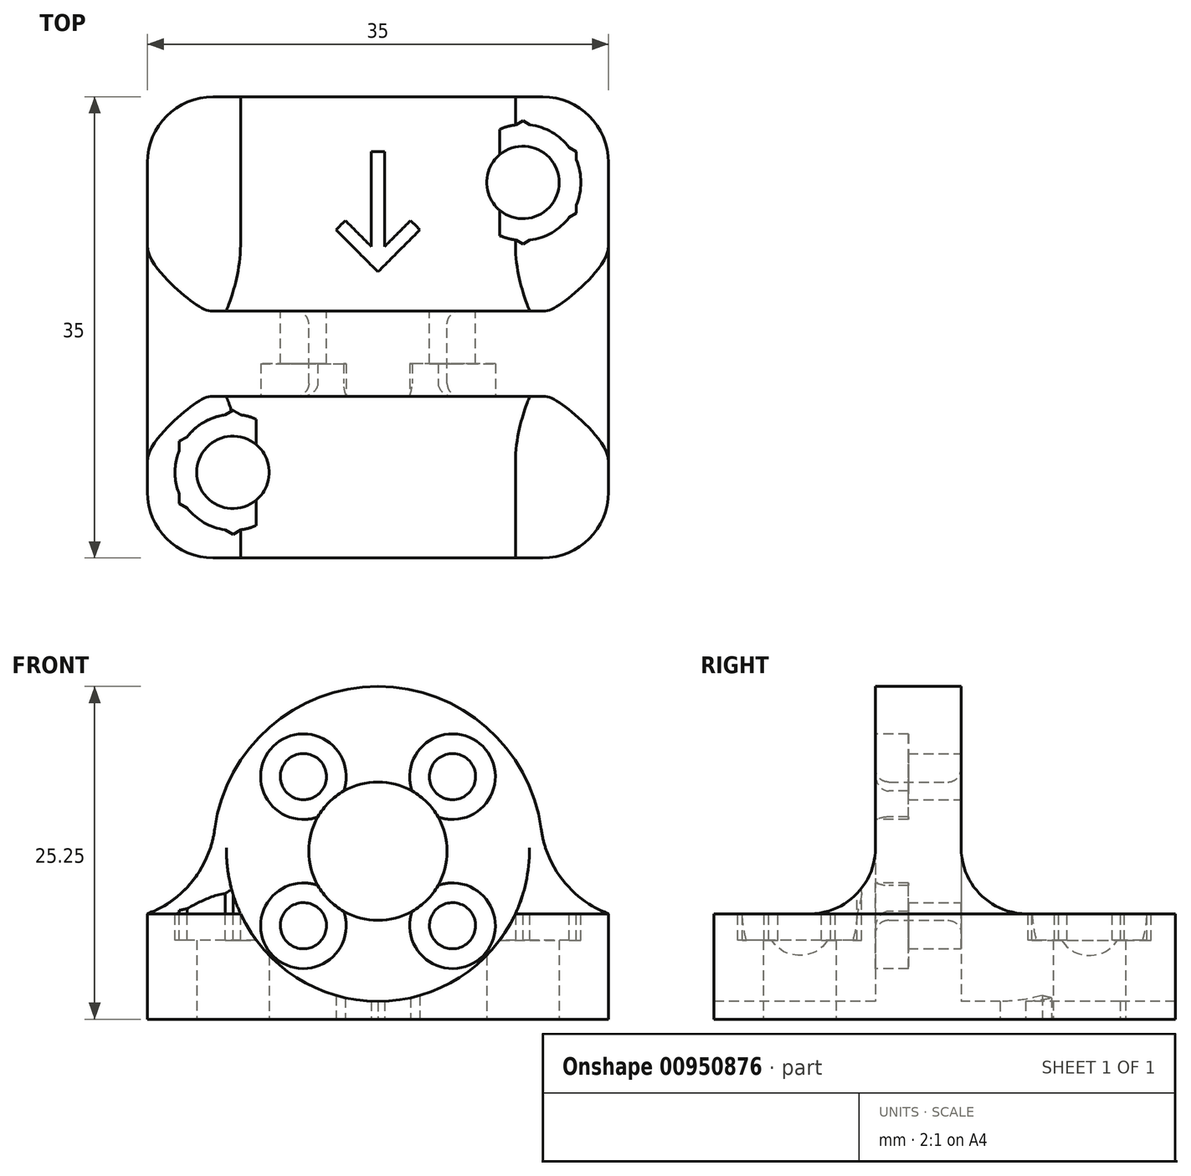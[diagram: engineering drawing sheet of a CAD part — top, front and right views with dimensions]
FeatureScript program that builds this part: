
annotation { "Feature Type Name" : "Feature", "Feature Type Description" : "" }
export const myFeature = defineFeature(function(context is Context, id is Id, definition is map)
    precondition{}
    {
        {
            var Q0;
            Q0=qCreatedBy(makeId("Front.planeOp"),FACE);
            cPlane(context, id + "F0", {"entities" : qUnion([Q0]), "cplaneType" : CPlaneType.OFFSET, "offset" : 2 * mm, "width" : 150 * mm, "height" : 150 * mm});
        }
        {
            var Q0;
            Q0=qCreatedBy(makeId("Top.planeOp"),FACE);
            var sketch = newSketch(context, id + "F1", { "sketchPlane" : qUnion([Q0])});
            skLineSegment(sketch, "E0.bottom", {"start": v(-17.5, 17.5) * mm, "end": v(17.5, 17.5) * mm});
            skLineSegment(sketch, "E0.top", {"start": v(-17.5, -17.5) * mm, "end": v(17.5, -17.5) * mm});
            skLineSegment(sketch, "E0.left", {"start": v(-17.5, 17.5) * mm, "end": v(-17.5, -17.5) * mm});
            skLineSegment(sketch, "E0.right", {"start": v(17.5, 17.5) * mm, "end": v(17.5, -17.5) * mm});
            skPoint(sketch, "E0.middle", {"position": v(0, 0) * mm});
            skLineSegment(sketch, "E1.bottom", {"start": v(-11, 11) * mm, "end": v(11, 11) * mm, "construction": true});
            skLineSegment(sketch, "E1.top", {"start": v(-11, -11) * mm, "end": v(11, -11) * mm, "construction": true});
            skLineSegment(sketch, "E1.left", {"start": v(-11, 11) * mm, "end": v(-11, -11) * mm, "construction": true});
            skLineSegment(sketch, "E1.right", {"start": v(11, 11) * mm, "end": v(11, -11) * mm, "construction": true});
            skCircle(sketch, "E2", {"center": v(-11, 11) * mm, "radius": 2.75 * mm, "construction": true});
            skCircle(sketch, "E3", {"center": v(11, 11) * mm, "radius": 2.75 * mm});
            skCircle(sketch, "E4", {"center": v(11, -11) * mm, "radius": 2.75 * mm, "construction": true});
            skCircle(sketch, "E5", {"center": v(-11, -11) * mm, "radius": 2.75 * mm});
            skSolve(sketch);
        }
        {
            var Q0;
            Q0=qSketchRegion(id+"F1",true);
            extrude(context, id + "F2", {"entities" : qUnion([Q0]), "depth" : 8 * mm, "offsetDistance" : 25 * mm});
        }
        {
            var Q0;
            Q0=qCreatedBy(id+"F0.planeOp",FACE);
            var sketch = newSketch(context, id + "F3", { "sketchPlane" : qUnion([Q0])});
            skLineSegment(sketch, "E6", {"start": v(0, 0) * mm, "end": v(0, 12.75) * mm, "construction": true});
            skArc(sketch, "E7", {"start": v(12.5, 12.75) * mm, "mid": v(0, 25.25) * mm, "end": v(-12.5, 12.75) * mm});
            skLineSegment(sketch, "E8", {"start": v(-12.5, 12.75) * mm, "end": v(-12.5, 0) * mm});
            skLineSegment(sketch, "E9.MirrorCS", {"start": v(12.5, 12.75) * mm, "end": v(12.5, 0) * mm});
            skCircle(sketch, "E10", {"center": v(0, 12.75) * mm, "radius": 5.25 * mm});
            skCircle(sketch, "E11", {"center": v(0, 12.75) * mm, "radius": 8 * mm, "construction": true});
            skLineSegment(sketch, "E12", {"start": v(0, 20.75) * mm, "end": v(0, 4.75) * mm, "construction": true});
            skPoint(sketch, "E12.startSnap0", {"position": v(0, 25.25) * mm});
            skLineSegment(sketch, "E13", {"start": v(-8, 12.75) * mm, "end": v(8, 12.75) * mm, "construction": true});
            skLineSegment(sketch, "E14", {"start": v(0, 12.75) * mm, "end": v(-5.66, 18.4) * mm, "construction": true});
            skLineSegment(sketch, "E15", {"start": v(0, 12.75) * mm, "end": v(-5.66, 7.1) * mm, "construction": true});
            skLineSegment(sketch, "E16.MirrorCS", {"start": v(0, 12.75) * mm, "end": v(5.66, 18.4) * mm, "construction": true});
            skLineSegment(sketch, "E17.MirrorCS", {"start": v(0, 12.75) * mm, "end": v(5.66, 7.1) * mm, "construction": true});
            skCircle(sketch, "E18", {"center": v(-5.66, 18.4) * mm, "radius": 1.75 * mm});
            skCircle(sketch, "E19", {"center": v(-5.66, 7.1) * mm, "radius": 1.75 * mm});
            skCircle(sketch, "E20", {"center": v(5.66, 7.1) * mm, "radius": 1.75 * mm});
            skCircle(sketch, "E21", {"center": v(5.66, 18.4) * mm, "radius": 1.75 * mm});
            skLineSegment(sketch, "E22", {"start": v(-12.5, 0) * mm, "end": v(12.5, 0) * mm});
            skSolve(sketch);
        }
        {
            var Q0;
            Q0=qCreatedBy(makeId("Front.planeOp"),FACE);
            var sketch = newSketch(context, id + "F4", { "sketchPlane" : qUnion([Q0])});
            skLineSegment(sketch, "E23", {"start": v(0, 0) * mm, "end": v(0, 12.85) * mm, "construction": true});
            skCircle(sketch, "E24", {"center": v(0, 12.85) * mm, "radius": 11.5 * mm});
            skSolve(sketch);
        }
        {
            var Q0;
            Q0=qSketchRegion(id+"F4",true);
            extrude(context, id + "F5", {"entities" : qUnion([Q0]), "operationType" : NewBodyOperationType.REMOVE, "endBound" : BoundingType.SYMMETRIC, "oppositeDirection" : true, "depth" : 36 * mm, "offsetDistance" : 25 * mm});
        }
        {
            var Q0;
            Q0 = qSketchRegion(id + "F3", true);
            extrude(context, id + "F6", {"entities" : qUnion([Q0]), "operationType" : NewBodyOperationType.ADD, "endBound" : BoundingType.SYMMETRIC, "depth" : 6.5 * mm, "offsetDistance" : 25 * mm});
        }
        {
            var Q0;
            {var subQ0=sQuery(id+"F1.wireOp",EDGE,"E4");var subQ1=sQuery(id+"F1.wireOp",EDGE,"E0.top");var subQ2=sQuery(id+"F1.wireOp",EDGE,"E0.right");var subQ3=sQuery(id+"F1.wireOp",EDGE,"E0.bottom");Q0=makeQuery(id+"F6.boolean.opBoolean","INTERSECT",EDGE,{"derivedFrom":[makeQuery(id+"F5.boolean.opBoolean","SPLIT",FACE,{"disambiguationData":[TD([makeQuery(id+"F2.opExtrude","SWEPT_FACE",FACE,{"disambiguationData":[OSD([subQ2])]})])],"derivedFrom":makeQuery(id+"F2.opExtrude","CAP_FACE",FACE,{"disambiguationData":[OSD([subQ3,subQ1,sQuery(id+"F1.wireOp",EDGE,"E0.left"),subQ2,sQuery(id+"F1.wireOp",EDGE,"E2"),subQ0])],"isStart":false})}),makeQuery(id+"F6.opExtrude","SWEPT_FACE",FACE,{"disambiguationData":[OSD([sQuery(id+"F3.wireOp",EDGE,"E9.MirrorCS")])]})]});}
            var Q1;
            {var subQ0=sQuery(id+"F1.wireOp",EDGE,"E2");var subQ1=sQuery(id+"F1.wireOp",EDGE,"E0.left");var subQ2=sQuery(id+"F1.wireOp",EDGE,"E0.top");var subQ3=sQuery(id+"F1.wireOp",EDGE,"E0.bottom");Q1=makeQuery(id+"F6.boolean.opBoolean","INTERSECT",EDGE,{"derivedFrom":[makeQuery(id+"F5.boolean.opBoolean","SPLIT",FACE,{"disambiguationData":[TD([makeQuery(id+"F2.opExtrude","SWEPT_FACE",FACE,{"disambiguationData":[OSD([subQ1])]})])],"derivedFrom":makeQuery(id+"F2.opExtrude","CAP_FACE",FACE,{"disambiguationData":[OSD([subQ3,subQ2,subQ1,sQuery(id+"F1.wireOp",EDGE,"E0.right"),subQ0,sQuery(id+"F1.wireOp",EDGE,"E4")])],"isStart":false})}),makeQuery(id+"F6.opExtrude","SWEPT_FACE",FACE,{"disambiguationData":[OSD([sQuery(id+"F3.wireOp",EDGE,"E8")])]})]});}
            fillet(context, id + "F7", {"entities" : qUnion([Q0, Q1]), "radius" : 8 * mm, "tangentPropagation" : true, "allowEdgeOverflow" : false});
        }
        {
            var Q0;
            {var subQ0=sQuery(id+"F1.wireOp",EDGE,"E2");var subQ1=sQuery(id+"F1.wireOp",EDGE,"E0.left");var subQ2=sQuery(id+"F1.wireOp",EDGE,"E0.top");var subQ3=sQuery(id+"F1.wireOp",EDGE,"E0.bottom");Q0=makeQuery(id+"F7.opFillet","SPLIT",FACE,{"disambiguationData":[OD(0.0)],"derivedFrom":makeQuery(id+"F5.boolean.opBoolean","SPLIT",FACE,{"disambiguationData":[TD([makeQuery(id+"F2.opExtrude","SWEPT_FACE",FACE,{"disambiguationData":[OSD([subQ1])]})])],"derivedFrom":makeQuery(id+"F2.opExtrude","CAP_FACE",FACE,{"disambiguationData":[OSD([subQ3,subQ2,subQ1,sQuery(id+"F1.wireOp",EDGE,"E0.right"),subQ0,sQuery(id+"F1.wireOp",EDGE,"E4")])],"isStart":false})})});}
            var sketch = newSketch(context, id + "F8", { "sketchPlane" : qUnion([Q0])});
            skPoint(sketch, "E25.0.midPoint.positionSnap0", {"position": v(5.2, -11) * mm});
            skLineSegment(sketch, "E26", {"start": v(17.5, 17.5) * mm, "end": v(-17.5, -17.5) * mm, "construction": true});
            skCircle(sketch, "E27.cCircle", {"center": v(11, 11) * mm, "radius": 4.05 * mm, "construction": true});
            skLineSegment(sketch, "E27.0", {"start": v(15.05, 13.34) * mm, "end": v(15.05, 8.66) * mm});
            skLineSegment(sketch, "E27.1", {"start": v(15.05, 8.66) * mm, "end": v(11, 6.32) * mm});
            skLineSegment(sketch, "E27.2", {"start": v(11, 6.32) * mm, "end": v(6.95, 8.66) * mm});
            skLineSegment(sketch, "E27.3", {"start": v(6.95, 8.66) * mm, "end": v(6.95, 13.34) * mm});
            skLineSegment(sketch, "E27.4", {"start": v(6.95, 13.34) * mm, "end": v(11, 15.68) * mm});
            skLineSegment(sketch, "E27.5", {"start": v(11, 15.68) * mm, "end": v(15.05, 13.34) * mm});
            skPoint(sketch, "E27.0.midPoint", {"position": v(15.05, 11) * mm});
            skCircle(sketch, "E28.cCircle", {"center": v(-11, -11) * mm, "radius": 4.08 * mm, "construction": true});
            skLineSegment(sketch, "E28.0", {"start": v(-11, -6.3) * mm, "end": v(-6.93, -8.65) * mm});
            skLineSegment(sketch, "E28.1", {"start": v(-6.93, -8.65) * mm, "end": v(-6.93, -13.35) * mm});
            skLineSegment(sketch, "E28.2", {"start": v(-6.93, -13.35) * mm, "end": v(-11, -15.7) * mm});
            skLineSegment(sketch, "E28.3", {"start": v(-11, -15.7) * mm, "end": v(-15.08, -13.35) * mm});
            skLineSegment(sketch, "E28.4", {"start": v(-15.07, -13.35) * mm, "end": v(-15.07, -8.65) * mm});
            skLineSegment(sketch, "E28.5", {"start": v(-15.07, -8.65) * mm, "end": v(-11, -6.3) * mm});
            skPoint(sketch, "E28.0.midPoint", {"position": v(-8.96, -7.47) * mm});
            skSolve(sketch);
        }
        {
            var Q0;
            Q0=qSketchRegion(id+"F8",true);
            extrude(context, id + "F9", {"entities" : qUnion([Q0]), "operationType" : NewBodyOperationType.REMOVE, "oppositeDirection" : true, "depth" : 2 * mm, "offsetDistance" : 25 * mm});
        }
        {
            var Q0;
            {var subQ0=sQuery(id+"F1.wireOp",EDGE,"E2");var subQ1=sQuery(id+"F1.wireOp",EDGE,"E0.left");var subQ2=sQuery(id+"F1.wireOp",EDGE,"E0.top");var subQ3=sQuery(id+"F1.wireOp",EDGE,"E0.bottom");Q0=makeQuery(id+"F7.opFillet","SPLIT",FACE,{"disambiguationData":[OD(0.0)],"derivedFrom":makeQuery(id+"F5.boolean.opBoolean","SPLIT",FACE,{"disambiguationData":[TD([makeQuery(id+"F2.opExtrude","SWEPT_FACE",FACE,{"disambiguationData":[OSD([subQ1])]})])],"derivedFrom":makeQuery(id+"F2.opExtrude","CAP_FACE",FACE,{"disambiguationData":[OSD([subQ3,subQ2,subQ1,sQuery(id+"F1.wireOp",EDGE,"E0.right"),subQ0,sQuery(id+"F1.wireOp",EDGE,"E4")])],"isStart":false})})});}
            var sketch = newSketch(context, id + "F10", { "sketchPlane" : qUnion([Q0])});
            skCircle(sketch, "E29", {"center": v(11, 11) * mm, "radius": 4.4 * mm});
            skCircle(sketch, "E30", {"center": v(-11, -11) * mm, "radius": 4.4 * mm});
            skSolve(sketch);
        }
        {
            var Q0;
            Q0=qSketchRegion(id+"F10",true);
            extrude(context, id + "F11", {"entities" : qUnion([Q0]), "operationType" : NewBodyOperationType.REMOVE, "oppositeDirection" : true, "depth" : 2 * mm, "offsetDistance" : 25 * mm});
        }
        {
            var Q0;
            {var subQ0=sQuery(id+"F1.wireOp",EDGE,"E4");var subQ1=sQuery(id+"F1.wireOp",EDGE,"E0.top");var subQ2=sQuery(id+"F1.wireOp",EDGE,"E0.right");var subQ3=sQuery(id+"F1.wireOp",EDGE,"E0.bottom");Q0=makeQuery(id+"F6.boolean.opBoolean","INTERSECT",EDGE,{"derivedFrom":[makeQuery(id+"F5.boolean.opBoolean","SPLIT",FACE,{"disambiguationData":[TD([makeQuery(id+"F2.opExtrude","SWEPT_FACE",FACE,{"disambiguationData":[OSD([subQ2])]})])],"derivedFrom":makeQuery(id+"F2.opExtrude","CAP_FACE",FACE,{"disambiguationData":[OSD([subQ3,subQ1,sQuery(id+"F1.wireOp",EDGE,"E0.left"),subQ2,sQuery(id+"F1.wireOp",EDGE,"E2"),subQ0])],"isStart":false})}),makeQuery(id+"F6.opExtrude","CAP_FACE",FACE,{"disambiguationData":[OSD([sQuery(id+"F3.wireOp",EDGE,"E7"),sQuery(id+"F3.wireOp",EDGE,"E8"),sQuery(id+"F3.wireOp",EDGE,"E9.MirrorCS"),sQuery(id+"F3.wireOp",EDGE,"E10"),sQuery(id+"F3.wireOp",EDGE,"E18"),sQuery(id+"F3.wireOp",EDGE,"E19"),sQuery(id+"F3.wireOp",EDGE,"E20"),sQuery(id+"F3.wireOp",EDGE,"E21"),sQuery(id+"F3.wireOp",EDGE,"E22")])],"isStart":true})]});}
            var Q1;
            {var subQ0=sQuery(id+"F1.wireOp",EDGE,"E2");var subQ1=sQuery(id+"F1.wireOp",EDGE,"E0.left");var subQ2=sQuery(id+"F1.wireOp",EDGE,"E0.top");var subQ3=sQuery(id+"F1.wireOp",EDGE,"E0.bottom");Q1=makeQuery(id+"F6.boolean.opBoolean","INTERSECT",EDGE,{"derivedFrom":[makeQuery(id+"F5.boolean.opBoolean","SPLIT",FACE,{"disambiguationData":[TD([makeQuery(id+"F2.opExtrude","SWEPT_FACE",FACE,{"disambiguationData":[OSD([subQ1])]})])],"derivedFrom":makeQuery(id+"F2.opExtrude","CAP_FACE",FACE,{"disambiguationData":[OSD([subQ3,subQ2,subQ1,sQuery(id+"F1.wireOp",EDGE,"E0.right"),subQ0,sQuery(id+"F1.wireOp",EDGE,"E4")])],"isStart":false})}),makeQuery(id+"F6.opExtrude","CAP_FACE",FACE,{"disambiguationData":[OSD([sQuery(id+"F3.wireOp",EDGE,"E7"),sQuery(id+"F3.wireOp",EDGE,"E8"),sQuery(id+"F3.wireOp",EDGE,"E9.MirrorCS"),sQuery(id+"F3.wireOp",EDGE,"E10"),sQuery(id+"F3.wireOp",EDGE,"E18"),sQuery(id+"F3.wireOp",EDGE,"E19"),sQuery(id+"F3.wireOp",EDGE,"E20"),sQuery(id+"F3.wireOp",EDGE,"E21"),sQuery(id+"F3.wireOp",EDGE,"E22")])],"isStart":true})]});}
            var Q2;
            {var subQ0=sQuery(id+"F1.wireOp",EDGE,"E2");var subQ1=sQuery(id+"F1.wireOp",EDGE,"E0.left");var subQ2=sQuery(id+"F1.wireOp",EDGE,"E0.top");var subQ3=sQuery(id+"F1.wireOp",EDGE,"E0.bottom");Q2=makeQuery(id+"F6.boolean.opBoolean","INTERSECT",EDGE,{"derivedFrom":[makeQuery(id+"F5.boolean.opBoolean","SPLIT",FACE,{"disambiguationData":[TD([makeQuery(id+"F2.opExtrude","SWEPT_FACE",FACE,{"disambiguationData":[OSD([subQ1])]})])],"derivedFrom":makeQuery(id+"F2.opExtrude","CAP_FACE",FACE,{"disambiguationData":[OSD([subQ3,subQ2,subQ1,sQuery(id+"F1.wireOp",EDGE,"E0.right"),subQ0,sQuery(id+"F1.wireOp",EDGE,"E4")])],"isStart":false})}),makeQuery(id+"F6.opExtrude","CAP_FACE",FACE,{"disambiguationData":[OSD([sQuery(id+"F3.wireOp",EDGE,"E7"),sQuery(id+"F3.wireOp",EDGE,"E8"),sQuery(id+"F3.wireOp",EDGE,"E9.MirrorCS"),sQuery(id+"F3.wireOp",EDGE,"E10"),sQuery(id+"F3.wireOp",EDGE,"E18"),sQuery(id+"F3.wireOp",EDGE,"E19"),sQuery(id+"F3.wireOp",EDGE,"E20"),sQuery(id+"F3.wireOp",EDGE,"E21"),sQuery(id+"F3.wireOp",EDGE,"E22")])],"isStart":false})]});}
            var Q3;
            {var subQ0=sQuery(id+"F1.wireOp",EDGE,"E4");var subQ1=sQuery(id+"F1.wireOp",EDGE,"E0.top");var subQ2=sQuery(id+"F1.wireOp",EDGE,"E0.right");var subQ3=sQuery(id+"F1.wireOp",EDGE,"E0.bottom");Q3=makeQuery(id+"F6.boolean.opBoolean","INTERSECT",EDGE,{"derivedFrom":[makeQuery(id+"F5.boolean.opBoolean","SPLIT",FACE,{"disambiguationData":[TD([makeQuery(id+"F2.opExtrude","SWEPT_FACE",FACE,{"disambiguationData":[OSD([subQ2])]})])],"derivedFrom":makeQuery(id+"F2.opExtrude","CAP_FACE",FACE,{"disambiguationData":[OSD([subQ3,subQ1,sQuery(id+"F1.wireOp",EDGE,"E0.left"),subQ2,sQuery(id+"F1.wireOp",EDGE,"E2"),subQ0])],"isStart":false})}),makeQuery(id+"F6.opExtrude","CAP_FACE",FACE,{"disambiguationData":[OSD([sQuery(id+"F3.wireOp",EDGE,"E7"),sQuery(id+"F3.wireOp",EDGE,"E8"),sQuery(id+"F3.wireOp",EDGE,"E9.MirrorCS"),sQuery(id+"F3.wireOp",EDGE,"E10"),sQuery(id+"F3.wireOp",EDGE,"E18"),sQuery(id+"F3.wireOp",EDGE,"E19"),sQuery(id+"F3.wireOp",EDGE,"E20"),sQuery(id+"F3.wireOp",EDGE,"E21"),sQuery(id+"F3.wireOp",EDGE,"E22")])],"isStart":false})]});}
            var Q4;
            Q4=makeQuery(id+"F2.opExtrude","SWEPT_EDGE",EDGE,{"disambiguationData":[OSD([sQuery(id+"F1.wireOp",EDGE,"E0.top"),sQuery(id+"F1.wireOp",EDGE,"E0.left")])]});
            var Q5;
            Q5=makeQuery(id+"F2.opExtrude","SWEPT_EDGE",EDGE,{"disambiguationData":[OSD([sQuery(id+"F1.wireOp",EDGE,"E0.bottom"),sQuery(id+"F1.wireOp",EDGE,"E0.left")])]});
            var Q6;
            Q6=makeQuery(id+"F2.opExtrude","SWEPT_EDGE",EDGE,{"disambiguationData":[OSD([sQuery(id+"F1.wireOp",EDGE,"E0.bottom"),sQuery(id+"F1.wireOp",EDGE,"E0.right")])]});
            var Q7;
            Q7=makeQuery(id+"F2.opExtrude","SWEPT_EDGE",EDGE,{"disambiguationData":[OSD([sQuery(id+"F1.wireOp",EDGE,"E0.top"),sQuery(id+"F1.wireOp",EDGE,"E0.right")])]});
            fillet(context, id + "F12", {"entities" : qUnion([Q0, Q1, Q2, Q3, Q4, Q5, Q6, Q7]), "radius" : 5 * mm, "tangentPropagation" : true, "allowEdgeOverflow" : false});
        }
        {
            var Q0;
            Q0=makeQuery(id+"F6.opExtrude","CAP_FACE",FACE,{"disambiguationData":[OSD([sQuery(id+"F3.wireOp",EDGE,"E7"),sQuery(id+"F3.wireOp",EDGE,"E8"),sQuery(id+"F3.wireOp",EDGE,"E9.MirrorCS"),sQuery(id+"F3.wireOp",EDGE,"E10"),sQuery(id+"F3.wireOp",EDGE,"E18"),sQuery(id+"F3.wireOp",EDGE,"E20"),sQuery(id+"F3.wireOp",EDGE,"E22")])],"isStart":false});
            var sketch = newSketch(context, id + "F13", { "sketchPlane" : qUnion([Q0])});
            skCircle(sketch, "E31", {"center": v(-5.66, 18.4) * mm, "radius": 3.25 * mm});
            skCircle(sketch, "E32", {"center": v(5.66, 7.1) * mm, "radius": 3.25 * mm});
            skLineSegment(sketch, "E33", {"start": v(0, 12.75) * mm, "end": v(12.71, 12.75) * mm, "construction": true});
            skCircle(sketch, "E34.MirrorC", {"center": v(5.66, 18.4) * mm, "radius": 3.25 * mm});
            skCircle(sketch, "E35.MirrorC", {"center": v(-5.66, 7.1) * mm, "radius": 3.25 * mm});
            skSolve(sketch);
        }
        {
            var Q0;
            Q0 = qSketchRegion(id + "F13", true);
            var Q1;
            Q1=makeQuery(id+"F6.opExtrude","CAP_FACE",FACE,{"disambiguationData":[OSD([sQuery(id+"F3.wireOp",EDGE,"E7"),sQuery(id+"F3.wireOp",EDGE,"E8"),sQuery(id+"F3.wireOp",EDGE,"E9.MirrorCS"),sQuery(id+"F3.wireOp",EDGE,"E10"),sQuery(id+"F3.wireOp",EDGE,"E18"),sQuery(id+"F3.wireOp",EDGE,"E20"),sQuery(id+"F3.wireOp",EDGE,"E22")])],"isStart":true});
            extrude(context, id + "F14", {"entities" : qUnion([Q0]), "operationType" : NewBodyOperationType.REMOVE, "oppositeDirection" : true, "depth" : 2.5 * mm, "endBoundEntityFace" : qUnion([Q1]), "hasOffset" : true, "offsetDistance" : 5 * mm, "offsetOppositeDirection" : true});
        }
        {
            var Q0;
            Q0=makeQuery(id+"F2.opExtrude","CAP_FACE",FACE,{"disambiguationData":[OSD([sQuery(id+"F1.wireOp",EDGE,"E0.bottom"),sQuery(id+"F1.wireOp",EDGE,"E0.top"),sQuery(id+"F1.wireOp",EDGE,"E0.left"),sQuery(id+"F1.wireOp",EDGE,"E0.right"),sQuery(id+"F1.wireOp",EDGE,"E3"),sQuery(id+"F1.wireOp",EDGE,"E5")])],"isStart":true});
            var sketch = newSketch(context, id + "F15", { "sketchPlane" : qUnion([Q0])});
            skLineSegment(sketch, "E36", {"start": v(0, 0) * mm, "end": v(0, -17.5) * mm, "construction": true});
            skLineSegment(sketch, "E37", {"start": v(0, -4.22) * mm, "end": v(-3.18, -7.4) * mm});
            skLineSegment(sketch, "E38", {"start": v(-3.18, -7.4) * mm, "end": v(-2.47, -8.1) * mm});
            skLineSegment(sketch, "E39", {"start": v(-2.47, -8.1) * mm, "end": v(-0.5, -6.13) * mm});
            skLineSegment(sketch, "E40", {"start": v(-0.5, -6.13) * mm, "end": v(-0.5, -13.33) * mm});
            skLineSegment(sketch, "E41", {"start": v(-0.5, -13.33) * mm, "end": v(0, -13.33) * mm});
            skLineSegment(sketch, "E42.MirrorCS", {"start": v(0.5, -13.33) * mm, "end": v(0, -13.33) * mm});
            skLineSegment(sketch, "E43.MirrorCS", {"start": v(3.18, -7.4) * mm, "end": v(2.47, -8.1) * mm});
            skLineSegment(sketch, "E44.MirrorCS", {"start": v(0.5, -6.13) * mm, "end": v(0.5, -13.33) * mm});
            skLineSegment(sketch, "E45.MirrorCS", {"start": v(2.47, -8.1) * mm, "end": v(0.5, -6.13) * mm});
            skLineSegment(sketch, "E46.MirrorCS", {"start": v(0, -4.22) * mm, "end": v(3.18, -7.4) * mm});
            skSolve(sketch);
        }
        {
            var Q0;
            Q0=qSketchRegion(id+"F15",true);
            extrude(context, id + "F16", {"entities" : qUnion([Q0]), "operationType" : NewBodyOperationType.REMOVE, "oppositeDirection" : true, "depth" : 3 * mm, "offsetDistance" : 25 * mm});
        }
        {
            var Q0;
            Q0=makeQuery(id+"F14.boolean.opBoolean","COPY",EDGE,{"derivedFrom":makeQuery(id+"F14.opExtrude","CAP_EDGE",EDGE,{"disambiguationData":[OSD([sQuery(id+"F13.wireOp",EDGE,"E31")])],"isStart":true})});
            var Q1;
            Q1=makeQuery(id+"F14.boolean.opBoolean","COPY",EDGE,{"derivedFrom":makeQuery(id+"F14.opExtrude","CAP_EDGE",EDGE,{"disambiguationData":[OSD([sQuery(id+"F13.wireOp",EDGE,"E34.MirrorC")])],"isStart":true})});
            var Q2;
            Q2=makeQuery(id+"F14.boolean.opBoolean","COPY",EDGE,{"derivedFrom":makeQuery(id+"F14.opExtrude","CAP_EDGE",EDGE,{"disambiguationData":[OSD([sQuery(id+"F13.wireOp",EDGE,"E32")])],"isStart":true})});
            var Q3;
            Q3=makeQuery(id+"F14.boolean.opBoolean","COPY",EDGE,{"derivedFrom":makeQuery(id+"F14.opExtrude","CAP_EDGE",EDGE,{"disambiguationData":[OSD([sQuery(id+"F13.wireOp",EDGE,"E35.MirrorC")])],"isStart":true})});
            var Q4;
            {var subQ0=sQuery(id+"F3.wireOp",EDGE,"E10");Q4=makeQuery(id+"F14.boolean.opBoolean","SPLIT",EDGE,{"disambiguationData":[TD([makeQuery(id+"F6.opExtrude","CAP_FACE",FACE,{"disambiguationData":[OSD([sQuery(id+"F3.wireOp",EDGE,"E7"),sQuery(id+"F3.wireOp",EDGE,"E8"),sQuery(id+"F3.wireOp",EDGE,"E9.MirrorCS"),subQ0,sQuery(id+"F3.wireOp",EDGE,"E18"),sQuery(id+"F3.wireOp",EDGE,"E19"),sQuery(id+"F3.wireOp",EDGE,"E20"),sQuery(id+"F3.wireOp",EDGE,"E21"),sQuery(id+"F3.wireOp",EDGE,"E22")])],"isStart":false}),makeQuery(id+"F6.opExtrude","SWEPT_FACE",FACE,{"disambiguationData":[OSD([subQ0])]}),makeQuery(id+"F14.opExtrude","SWEPT_FACE",FACE,{"disambiguationData":[OSD([sQuery(id+"F13.wireOp",EDGE,"E31")])]}),makeQuery(id+"F14.opExtrude","SWEPT_FACE",FACE,{"disambiguationData":[OSD([sQuery(id+"F13.wireOp",EDGE,"E35.MirrorC")])]})])],"derivedFrom":makeQuery(id+"F6.opExtrude","CAP_EDGE",EDGE,{"disambiguationData":[OSD([subQ0])],"isStart":false})});}
            var Q5;
            {var subQ0=sQuery(id+"F3.wireOp",EDGE,"E10");Q5=makeQuery(id+"F14.boolean.opBoolean","SPLIT",EDGE,{"disambiguationData":[TD([makeQuery(id+"F6.opExtrude","CAP_FACE",FACE,{"disambiguationData":[OSD([sQuery(id+"F3.wireOp",EDGE,"E7"),sQuery(id+"F3.wireOp",EDGE,"E8"),sQuery(id+"F3.wireOp",EDGE,"E9.MirrorCS"),subQ0,sQuery(id+"F3.wireOp",EDGE,"E18"),sQuery(id+"F3.wireOp",EDGE,"E19"),sQuery(id+"F3.wireOp",EDGE,"E20"),sQuery(id+"F3.wireOp",EDGE,"E21"),sQuery(id+"F3.wireOp",EDGE,"E22")])],"isStart":false}),makeQuery(id+"F6.opExtrude","SWEPT_FACE",FACE,{"disambiguationData":[OSD([subQ0])]}),makeQuery(id+"F14.opExtrude","SWEPT_FACE",FACE,{"disambiguationData":[OSD([sQuery(id+"F13.wireOp",EDGE,"E31")])]}),makeQuery(id+"F14.opExtrude","SWEPT_FACE",FACE,{"disambiguationData":[OSD([sQuery(id+"F13.wireOp",EDGE,"E34.MirrorC")])]})])],"derivedFrom":makeQuery(id+"F6.opExtrude","CAP_EDGE",EDGE,{"disambiguationData":[OSD([subQ0])],"isStart":false})});}
            var Q6;
            {var subQ0=sQuery(id+"F3.wireOp",EDGE,"E10");Q6=makeQuery(id+"F14.boolean.opBoolean","SPLIT",EDGE,{"disambiguationData":[TD([makeQuery(id+"F6.opExtrude","CAP_FACE",FACE,{"disambiguationData":[OSD([sQuery(id+"F3.wireOp",EDGE,"E7"),sQuery(id+"F3.wireOp",EDGE,"E8"),sQuery(id+"F3.wireOp",EDGE,"E9.MirrorCS"),subQ0,sQuery(id+"F3.wireOp",EDGE,"E18"),sQuery(id+"F3.wireOp",EDGE,"E19"),sQuery(id+"F3.wireOp",EDGE,"E20"),sQuery(id+"F3.wireOp",EDGE,"E21"),sQuery(id+"F3.wireOp",EDGE,"E22")])],"isStart":false}),makeQuery(id+"F6.opExtrude","SWEPT_FACE",FACE,{"disambiguationData":[OSD([subQ0])]}),makeQuery(id+"F14.opExtrude","SWEPT_FACE",FACE,{"disambiguationData":[OSD([sQuery(id+"F13.wireOp",EDGE,"E32")])]}),makeQuery(id+"F14.opExtrude","SWEPT_FACE",FACE,{"disambiguationData":[OSD([sQuery(id+"F13.wireOp",EDGE,"E34.MirrorC")])]})])],"derivedFrom":makeQuery(id+"F6.opExtrude","CAP_EDGE",EDGE,{"disambiguationData":[OSD([subQ0])],"isStart":false})});}
            var Q7;
            {var subQ0=sQuery(id+"F3.wireOp",EDGE,"E10");Q7=makeQuery(id+"F14.boolean.opBoolean","SPLIT",EDGE,{"disambiguationData":[TD([makeQuery(id+"F6.opExtrude","CAP_FACE",FACE,{"disambiguationData":[OSD([sQuery(id+"F3.wireOp",EDGE,"E7"),sQuery(id+"F3.wireOp",EDGE,"E8"),sQuery(id+"F3.wireOp",EDGE,"E9.MirrorCS"),subQ0,sQuery(id+"F3.wireOp",EDGE,"E18"),sQuery(id+"F3.wireOp",EDGE,"E19"),sQuery(id+"F3.wireOp",EDGE,"E20"),sQuery(id+"F3.wireOp",EDGE,"E21"),sQuery(id+"F3.wireOp",EDGE,"E22")])],"isStart":false}),makeQuery(id+"F6.opExtrude","SWEPT_FACE",FACE,{"disambiguationData":[OSD([subQ0])]}),makeQuery(id+"F14.opExtrude","SWEPT_FACE",FACE,{"disambiguationData":[OSD([sQuery(id+"F13.wireOp",EDGE,"E32")])]}),makeQuery(id+"F14.opExtrude","SWEPT_FACE",FACE,{"disambiguationData":[OSD([sQuery(id+"F13.wireOp",EDGE,"E35.MirrorC")])]})])],"derivedFrom":makeQuery(id+"F6.opExtrude","CAP_EDGE",EDGE,{"disambiguationData":[OSD([subQ0])],"isStart":false})});}
            var Q8;
            Q8=makeQuery(id+"F6.opExtrude","CAP_EDGE",EDGE,{"disambiguationData":[OSD([sQuery(id+"F3.wireOp",EDGE,"E10")])],"isStart":true});
            fillet(context, id + "F17", {"entities" : qUnion([Q0, Q1, Q2, Q3, Q4, Q5, Q6, Q7, Q8]), "radius" : 1 * mm, "tangentPropagation" : true, "allowEdgeOverflow" : false});
        }
    });
